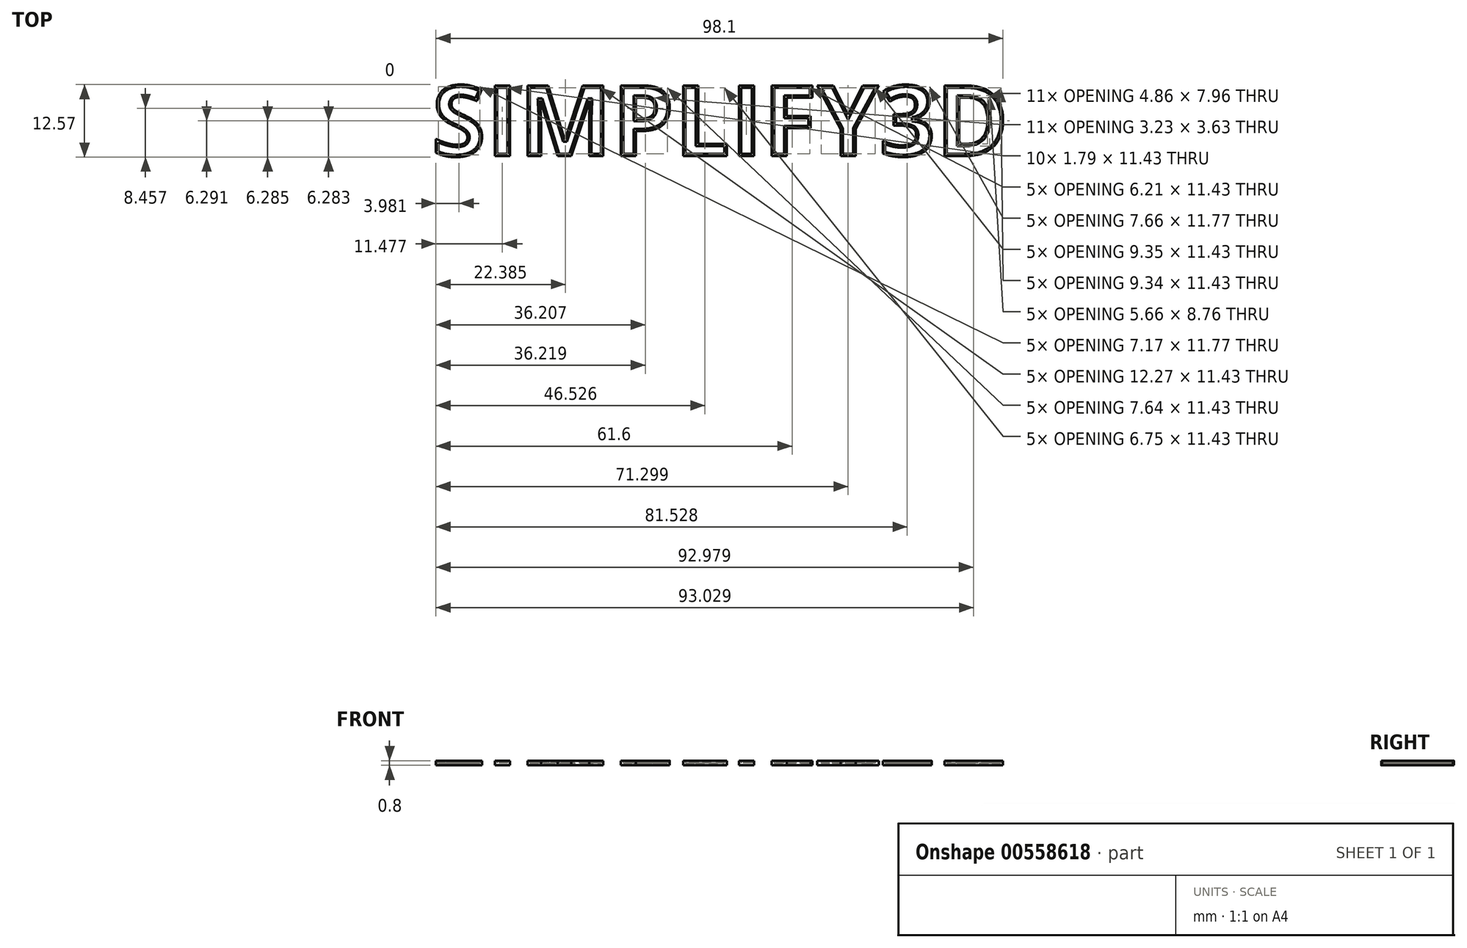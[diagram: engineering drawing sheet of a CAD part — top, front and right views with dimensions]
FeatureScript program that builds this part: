
annotation { "Feature Type Name" : "Feature", "Feature Type Description" : "" }
export const myFeature = defineFeature(function(context is Context, id is Id, definition is map)
    precondition{}
    {
        {
            var Q0;
            Q0=qCreatedBy(makeId("Top.planeOp"),FACE);
            var sketch = newSketch(context, id + "F0", { "sketchPlane" : qUnion([Q0])});
            skText(sketch, "E0", { "text": "SIMPLIFY3D", "fontName": "OpenSans-Bold.ttf"});
            const initialGuessF0  = {"E0": [0, 0, 1, 0, 0.01233]};
            skSetInitialGuess(sketch, initialGuessF0);
            skSolve(sketch);
        }
        {
            var Q0;
            Q0 = qSketchRegion(id + "F0", true);
            extrude(context, id + "F1", {"entities" : qUnion([Q0]), "depth" : .8 * mm, "offsetDistance" : 25 * mm});
        }
        {
            var Q0;
            Q0=makeQuery(id+"F1.opExtrude","CAP_FACE",FACE,{"disambiguationData":[OSD([sQuery(id+"F0.wireOp",EDGE,"E0.sketch_text.stroke-0"),sQuery(id+"F0.wireOp",EDGE,"E0.sketch_text.stroke-1"),sQuery(id+"F0.wireOp",EDGE,"E0.sketch_text.stroke-2"),sQuery(id+"F0.wireOp",EDGE,"E0.sketch_text.stroke-3"),sQuery(id+"F0.wireOp",EDGE,"E0.sketch_text.stroke-4"),sQuery(id+"F0.wireOp",EDGE,"E0.sketch_text.stroke-5"),sQuery(id+"F0.wireOp",EDGE,"E0.sketch_text.stroke-6"),sQuery(id+"F0.wireOp",EDGE,"E0.sketch_text.stroke-7"),sQuery(id+"F0.wireOp",EDGE,"E0.sketch_text.stroke-8"),sQuery(id+"F0.wireOp",EDGE,"E0.sketch_text.stroke-9"),sQuery(id+"F0.wireOp",EDGE,"E0.sketch_text.stroke-10"),sQuery(id+"F0.wireOp",EDGE,"E0.sketch_text.stroke-11"),sQuery(id+"F0.wireOp",EDGE,"E0.sketch_text.stroke-12"),sQuery(id+"F0.wireOp",EDGE,"E0.sketch_text.stroke-13"),sQuery(id+"F0.wireOp",EDGE,"E0.sketch_text.stroke-14"),sQuery(id+"F0.wireOp",EDGE,"E0.sketch_text.stroke-15"),sQuery(id+"F0.wireOp",EDGE,"E0.sketch_text.stroke-16"),sQuery(id+"F0.wireOp",EDGE,"E0.sketch_text.stroke-17"),sQuery(id+"F0.wireOp",EDGE,"E0.sketch_text.stroke-18"),sQuery(id+"F0.wireOp",EDGE,"E0.sketch_text.stroke-19"),sQuery(id+"F0.wireOp",EDGE,"E0.sketch_text.stroke-20"),sQuery(id+"F0.wireOp",EDGE,"E0.sketch_text.stroke-21"),sQuery(id+"F0.wireOp",EDGE,"E0.sketch_text.stroke-22"),sQuery(id+"F0.wireOp",EDGE,"E0.sketch_text.stroke-23"),sQuery(id+"F0.wireOp",EDGE,"E0.sketch_text.stroke-24"),sQuery(id+"F0.wireOp",EDGE,"E0.sketch_text.stroke-25"),sQuery(id+"F0.wireOp",EDGE,"E0.sketch_text.stroke-26"),sQuery(id+"F0.wireOp",EDGE,"E0.sketch_text.stroke-27")])],"isStart":false});
            var Q1;
            Q1=makeQuery(id+"F1.opExtrude","CAP_FACE",FACE,{"disambiguationData":[OSD([sQuery(id+"F0.wireOp",EDGE,"E0.sketch_text.stroke-28"),sQuery(id+"F0.wireOp",EDGE,"E0.sketch_text.stroke-29"),sQuery(id+"F0.wireOp",EDGE,"E0.sketch_text.stroke-30"),sQuery(id+"F0.wireOp",EDGE,"E0.sketch_text.stroke-31")])],"isStart":false});
            var Q2;
            Q2=makeQuery(id+"F1.opExtrude","CAP_FACE",FACE,{"disambiguationData":[OSD([sQuery(id+"F0.wireOp",EDGE,"E0.sketch_text.stroke-32"),sQuery(id+"F0.wireOp",EDGE,"E0.sketch_text.stroke-33"),sQuery(id+"F0.wireOp",EDGE,"E0.sketch_text.stroke-34"),sQuery(id+"F0.wireOp",EDGE,"E0.sketch_text.stroke-35"),sQuery(id+"F0.wireOp",EDGE,"E0.sketch_text.stroke-36"),sQuery(id+"F0.wireOp",EDGE,"E0.sketch_text.stroke-37"),sQuery(id+"F0.wireOp",EDGE,"E0.sketch_text.stroke-38"),sQuery(id+"F0.wireOp",EDGE,"E0.sketch_text.stroke-39"),sQuery(id+"F0.wireOp",EDGE,"E0.sketch_text.stroke-40"),sQuery(id+"F0.wireOp",EDGE,"E0.sketch_text.stroke-41"),sQuery(id+"F0.wireOp",EDGE,"E0.sketch_text.stroke-42"),sQuery(id+"F0.wireOp",EDGE,"E0.sketch_text.stroke-43"),sQuery(id+"F0.wireOp",EDGE,"E0.sketch_text.stroke-44"),sQuery(id+"F0.wireOp",EDGE,"E0.sketch_text.stroke-45"),sQuery(id+"F0.wireOp",EDGE,"E0.sketch_text.stroke-46"),sQuery(id+"F0.wireOp",EDGE,"E0.sketch_text.stroke-47"),sQuery(id+"F0.wireOp",EDGE,"E0.sketch_text.stroke-48"),sQuery(id+"F0.wireOp",EDGE,"E0.sketch_text.stroke-49"),sQuery(id+"F0.wireOp",EDGE,"E0.sketch_text.stroke-50")])],"isStart":false});
            var Q3;
            Q3=makeQuery(id+"F1.opExtrude","CAP_FACE",FACE,{"disambiguationData":[OSD([sQuery(id+"F0.wireOp",EDGE,"E0.sketch_text.stroke-51"),sQuery(id+"F0.wireOp",EDGE,"E0.sketch_text.stroke-52"),sQuery(id+"F0.wireOp",EDGE,"E0.sketch_text.stroke-53"),sQuery(id+"F0.wireOp",EDGE,"E0.sketch_text.stroke-54"),sQuery(id+"F0.wireOp",EDGE,"E0.sketch_text.stroke-55"),sQuery(id+"F0.wireOp",EDGE,"E0.sketch_text.stroke-56"),sQuery(id+"F0.wireOp",EDGE,"E0.sketch_text.stroke-57"),sQuery(id+"F0.wireOp",EDGE,"E0.sketch_text.stroke-58"),sQuery(id+"F0.wireOp",EDGE,"E0.sketch_text.stroke-59"),sQuery(id+"F0.wireOp",EDGE,"E0.sketch_text.stroke-60"),sQuery(id+"F0.wireOp",EDGE,"E0.sketch_text.stroke-61"),sQuery(id+"F0.wireOp",EDGE,"E0.sketch_text.stroke-62"),sQuery(id+"F0.wireOp",EDGE,"E0.sketch_text.stroke-63"),sQuery(id+"F0.wireOp",EDGE,"E0.sketch_text.stroke-64"),sQuery(id+"F0.wireOp",EDGE,"E0.sketch_text.stroke-65"),sQuery(id+"F0.wireOp",EDGE,"E0.sketch_text.stroke-66")])],"isStart":false});
            var Q4;
            Q4=makeQuery(id+"F1.opExtrude","CAP_FACE",FACE,{"disambiguationData":[OSD([sQuery(id+"F0.wireOp",EDGE,"E0.sketch_text.stroke-67"),sQuery(id+"F0.wireOp",EDGE,"E0.sketch_text.stroke-68"),sQuery(id+"F0.wireOp",EDGE,"E0.sketch_text.stroke-69"),sQuery(id+"F0.wireOp",EDGE,"E0.sketch_text.stroke-70"),sQuery(id+"F0.wireOp",EDGE,"E0.sketch_text.stroke-71"),sQuery(id+"F0.wireOp",EDGE,"E0.sketch_text.stroke-72")])],"isStart":false});
            var Q5;
            Q5=makeQuery(id+"F1.opExtrude","CAP_FACE",FACE,{"disambiguationData":[OSD([sQuery(id+"F0.wireOp",EDGE,"E0.sketch_text.stroke-73"),sQuery(id+"F0.wireOp",EDGE,"E0.sketch_text.stroke-74"),sQuery(id+"F0.wireOp",EDGE,"E0.sketch_text.stroke-75"),sQuery(id+"F0.wireOp",EDGE,"E0.sketch_text.stroke-76")])],"isStart":false});
            var Q6;
            Q6=makeQuery(id+"F1.opExtrude","CAP_FACE",FACE,{"disambiguationData":[OSD([sQuery(id+"F0.wireOp",EDGE,"E0.sketch_text.stroke-77"),sQuery(id+"F0.wireOp",EDGE,"E0.sketch_text.stroke-78"),sQuery(id+"F0.wireOp",EDGE,"E0.sketch_text.stroke-79"),sQuery(id+"F0.wireOp",EDGE,"E0.sketch_text.stroke-80"),sQuery(id+"F0.wireOp",EDGE,"E0.sketch_text.stroke-81"),sQuery(id+"F0.wireOp",EDGE,"E0.sketch_text.stroke-82"),sQuery(id+"F0.wireOp",EDGE,"E0.sketch_text.stroke-83"),sQuery(id+"F0.wireOp",EDGE,"E0.sketch_text.stroke-84"),sQuery(id+"F0.wireOp",EDGE,"E0.sketch_text.stroke-85"),sQuery(id+"F0.wireOp",EDGE,"E0.sketch_text.stroke-86")])],"isStart":false});
            var Q7;
            Q7=makeQuery(id+"F1.opExtrude","CAP_FACE",FACE,{"disambiguationData":[OSD([sQuery(id+"F0.wireOp",EDGE,"E0.sketch_text.stroke-87"),sQuery(id+"F0.wireOp",EDGE,"E0.sketch_text.stroke-88"),sQuery(id+"F0.wireOp",EDGE,"E0.sketch_text.stroke-89"),sQuery(id+"F0.wireOp",EDGE,"E0.sketch_text.stroke-90"),sQuery(id+"F0.wireOp",EDGE,"E0.sketch_text.stroke-91"),sQuery(id+"F0.wireOp",EDGE,"E0.sketch_text.stroke-92"),sQuery(id+"F0.wireOp",EDGE,"E0.sketch_text.stroke-93"),sQuery(id+"F0.wireOp",EDGE,"E0.sketch_text.stroke-94"),sQuery(id+"F0.wireOp",EDGE,"E0.sketch_text.stroke-95")])],"isStart":false});
            var Q8;
            Q8=makeQuery(id+"F1.opExtrude","CAP_FACE",FACE,{"disambiguationData":[OSD([sQuery(id+"F0.wireOp",EDGE,"E0.sketch_text.stroke-96"),sQuery(id+"F0.wireOp",EDGE,"E0.sketch_text.stroke-97"),sQuery(id+"F0.wireOp",EDGE,"E0.sketch_text.stroke-98"),sQuery(id+"F0.wireOp",EDGE,"E0.sketch_text.stroke-99"),sQuery(id+"F0.wireOp",EDGE,"E0.sketch_text.stroke-100"),sQuery(id+"F0.wireOp",EDGE,"E0.sketch_text.stroke-101"),sQuery(id+"F0.wireOp",EDGE,"E0.sketch_text.stroke-102"),sQuery(id+"F0.wireOp",EDGE,"E0.sketch_text.stroke-103"),sQuery(id+"F0.wireOp",EDGE,"E0.sketch_text.stroke-104"),sQuery(id+"F0.wireOp",EDGE,"E0.sketch_text.stroke-105"),sQuery(id+"F0.wireOp",EDGE,"E0.sketch_text.stroke-106"),sQuery(id+"F0.wireOp",EDGE,"E0.sketch_text.stroke-107"),sQuery(id+"F0.wireOp",EDGE,"E0.sketch_text.stroke-108"),sQuery(id+"F0.wireOp",EDGE,"E0.sketch_text.stroke-109"),sQuery(id+"F0.wireOp",EDGE,"E0.sketch_text.stroke-110"),sQuery(id+"F0.wireOp",EDGE,"E0.sketch_text.stroke-111"),sQuery(id+"F0.wireOp",EDGE,"E0.sketch_text.stroke-112"),sQuery(id+"F0.wireOp",EDGE,"E0.sketch_text.stroke-113"),sQuery(id+"F0.wireOp",EDGE,"E0.sketch_text.stroke-114"),sQuery(id+"F0.wireOp",EDGE,"E0.sketch_text.stroke-115"),sQuery(id+"F0.wireOp",EDGE,"E0.sketch_text.stroke-116"),sQuery(id+"F0.wireOp",EDGE,"E0.sketch_text.stroke-117"),sQuery(id+"F0.wireOp",EDGE,"E0.sketch_text.stroke-118"),sQuery(id+"F0.wireOp",EDGE,"E0.sketch_text.stroke-119"),sQuery(id+"F0.wireOp",EDGE,"E0.sketch_text.stroke-120"),sQuery(id+"F0.wireOp",EDGE,"E0.sketch_text.stroke-121"),sQuery(id+"F0.wireOp",EDGE,"E0.sketch_text.stroke-122")])],"isStart":false});
            var Q9;
            Q9=makeQuery(id+"F1.opExtrude","CAP_FACE",FACE,{"disambiguationData":[OSD([sQuery(id+"F0.wireOp",EDGE,"E0.sketch_text.stroke-123"),sQuery(id+"F0.wireOp",EDGE,"E0.sketch_text.stroke-124"),sQuery(id+"F0.wireOp",EDGE,"E0.sketch_text.stroke-125"),sQuery(id+"F0.wireOp",EDGE,"E0.sketch_text.stroke-126"),sQuery(id+"F0.wireOp",EDGE,"E0.sketch_text.stroke-127"),sQuery(id+"F0.wireOp",EDGE,"E0.sketch_text.stroke-128"),sQuery(id+"F0.wireOp",EDGE,"E0.sketch_text.stroke-129"),sQuery(id+"F0.wireOp",EDGE,"E0.sketch_text.stroke-130"),sQuery(id+"F0.wireOp",EDGE,"E0.sketch_text.stroke-131"),sQuery(id+"F0.wireOp",EDGE,"E0.sketch_text.stroke-132"),sQuery(id+"F0.wireOp",EDGE,"E0.sketch_text.stroke-133"),sQuery(id+"F0.wireOp",EDGE,"E0.sketch_text.stroke-134")])],"isStart":false});
            shell(context, id + "F2", {"entities" : qUnion([Q0, Q1, Q2, Q3, Q4, Q5, Q6, Q7, Q8, Q9]), "thickness" : .4 * mm});
        }
    });
